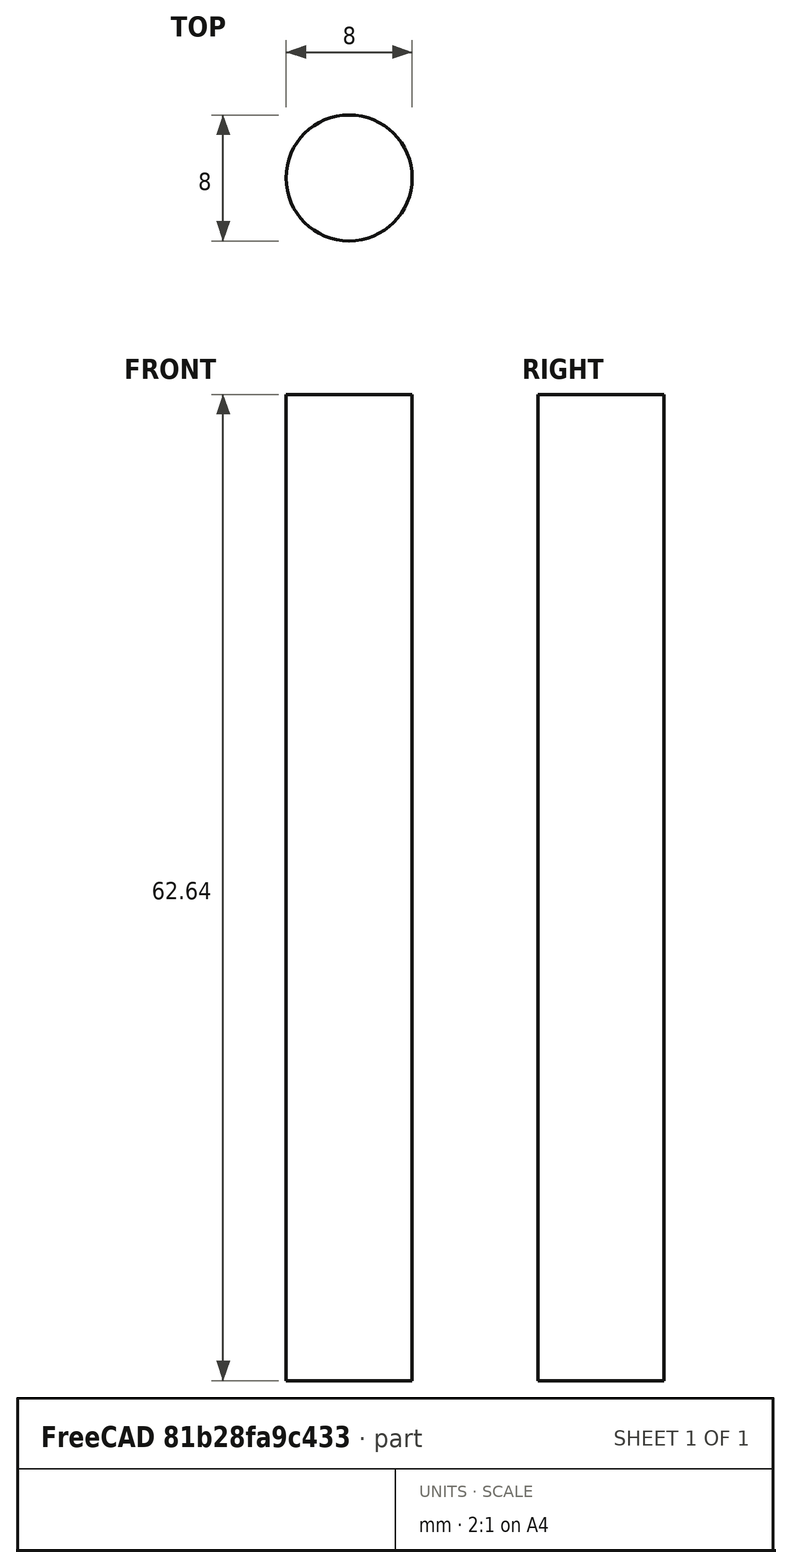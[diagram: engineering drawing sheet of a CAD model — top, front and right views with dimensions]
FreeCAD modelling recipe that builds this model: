
FCSTD DOCUMENT  (FreeCAD 1.0R39109 (Git))
Label: Studs_Frame_Base
License: All rights reserved
LicenseURL: http://en.wikipedia.org/wiki/All_rights_reserved
objects: App::Link×6, Spreadsheet::Sheet×1, Part::Cylinder×1, App::Part×1
note: 1 computed .brp shape members not serialized (recipe doc carries the construction recipe); baked Part::Feature solids carry a one-line shape summary decoded from their .brp
EXTERNAL_REF file=../../Master_of_Puppets.FCStd obj=Alternator
EXTERNAL_REF file=../../Master_of_Puppets.FCStd obj=Fastener
EXTERNAL_REF file=../../Master_of_Puppets.FCStd obj=Hub
EXTERNAL_REF file=../../Master_of_Puppets.FCStd obj=Spreadsheet
EXTERNAL_REF file=../../Fasteners/Fastener_HexNut.FCStd obj=Body
EXTERNAL_REF file=../../Fasteners/Fastener_Washer.FCStd obj=Tube

FEATURE [Spreadsheet::Sheet] Spreadsheet
  cells = A1='Inputs; A2='HolesRadius; B2(HolesRadius)==Master_of_Puppets#Alternator.HolesRadius; A3='MetalThicknessL; B3(MetalThicknessL)==Master_of_Puppets#Spreadsheet.MetalThicknessL; A4='MetalLengthL; B4(MetalLengthL)==Master_of_Puppets#Spreadsheet.MetalLengthL; A5='StatorMountingStudsLength; B5(StatorMountingStudsLength)==Master_of_Puppets#Alternator.StatorMountingStudsLength; A6='StatorThickness; B6(StatorThickness)==Master_of_Puppets#Spreadsheet.StatorThickness; A7='MechanicalClearance; B7(MechanicalClearance)==Master_of_Puppets#Spreadsheet.MechanicalClearance; A8='MagnetThickness; B8(MagnetThickness)==Master_of_Puppets#Spreadsheet.MagnetThickness; A9='RotorDiskThickness; B9(RotorDiskThickness)==Master_of_Puppets#Spreadsheet.RotorDiskThickness; A10='MiddlePadThickness; B10(MiddlePadThickness)==Master_of_Puppets#Hub.MiddlePadThickness; A11='HexNutThickness; B11(HexNutThickness)==Master_of_Puppets#Fastener.HexNutThickness; A12='WasherThickness; B12(WasherThickness)==Master_of_Puppets#Fastener.WasherThickness; A13='DistanceThreadsExtendFromNuts; B13(DistanceThreadsExtendFromNuts)==Master_of_Puppets#Fastener.DistanceThreadsExtendFromNuts; A14='RotorThickness; B14(RotorThickness)==Master_of_Puppets#Alternator.RotorThickness; A15='DistanceBetweenStatorAndFrame; B15(DistanceBetweenStatorAndFrame)==Master_of_Puppets#Alternator.DistanceBetweenStatorAndFrame; A16='Calculated; A17='DistanceBehindFrameBrackets; B17(DistanceBehindFrameBrackets)==MetalLengthL - MetalThicknessL; A18='BackFrameZ; B18(BackFrameZ)==StatorMountingStudsLength - DistanceBehindFrameBrackets; A19='FrontFrameZ; B19(FrontFrameZ)==BackFrameZ - HexNutThickness - MetalThicknessL; A20='BackStatorWasherZ; B20(BackStatorWasherZ)==BackFrameZ - MetalThicknessL - DistanceBetweenStatorAndFrame; A21='FrontStatorWasherZ; B21(FrontStatorWasherZ)==BackStatorWasherZ - StatorThickness - WasherThickness; A22='BackStatorHexNutZ; B22(BackStatorHexNutZ)==BackFrameZ - MetalThicknessL - DistanceBetweenStatorAndFrame + WasherThickness; A23='FrontStatorHexNutZ; B23(FrontStatorHexNutZ)==BackStatorWasherZ - StatorThickness - HexNutThickness - WasherThickness; A24='StudZ; B24(StudZ)==-DistanceBehindFrameBrackets + HexNutThickness + DistanceThreadsExtendFromNuts
FEATURE [Part::Cylinder] Cylinder  label="Stud"
  Angle = 360
  AttacherType = Attacher::AttachEngine3D
  FirstAngle = 0
  Height = 62.64
  Placement = pos=(0,0,-23.09) rot=(0,0,1;0rad)
  Radius = 4
  SecondAngle = 0
  expr: .Placement.Base.z = Spreadsheet.StudZ
  expr: Height = Spreadsheet.StatorMountingStudsLength
  expr: Radius = Spreadsheet.HolesRadius
FEATURE [App::Link] Link  label="HexNut_Frame_Back"
  LinkPlacement = pos=(0,0,27.64) rot=(0,0,1;0rad)
  LinkedObject = -> <external ../../Fasteners/Fastener_HexNut.FCStd>#Body
  Placement = pos=(0,0,27.64) rot=(0,0,1;0rad)
  expr: .Placement.Base.z = Spreadsheet.BackFrameZ
FEATURE [App::Link] Link001  label="HexNut_Frame_Front"
  LinkPlacement = pos=(0,0,15.73) rot=(0,0,1;0rad)
  LinkedObject = -> <external ../../Fasteners/Fastener_HexNut.FCStd>#Body
  Placement = pos=(0,0,15.73) rot=(0,0,1;0rad)
  expr: .Placement.Base.z = Spreadsheet.FrontFrameZ
FEATURE [App::Link] Link002  label="HexNut_Stator_Back"
  LinkPlacement = pos=(0,0,3.82) rot=(0,0,1;0rad)
  LinkedObject = -> <external ../../Fasteners/Fastener_HexNut.FCStd>#Body
  Placement = pos=(0,0,3.82) rot=(0,0,1;0rad)
  expr: .Placement.Base.z = Spreadsheet.BackStatorHexNutZ
FEATURE [App::Link] Link003  label="HexNut_Stator_Front"
  LinkPlacement = pos=(0,0,-18.09) rot=(0,0,1;0rad)
  LinkedObject = -> <external ../../Fasteners/Fastener_HexNut.FCStd>#Body
  Placement = pos=(0,0,-18.09) rot=(0,0,1;0rad)
  expr: .Placement.Base.z = Spreadsheet.FrontStatorHexNutZ
FEATURE [App::Link] Link004  label="Washer_Stator_Back"
  LinkPlacement = pos=(0,0,1.32) rot=(0,0,1;0rad)
  LinkedObject = -> <external ../../Fasteners/Fastener_Washer.FCStd>#Tube
  Placement = pos=(0,0,1.32) rot=(0,0,1;0rad)
  expr: .Placement.Base.z = Spreadsheet.BackStatorWasherZ
FEATURE [App::Link] Link005  label="Washer_Stator_Front"
  LinkPlacement = pos=(0,0,-11.18) rot=(0,0,1;0rad)
  LinkedObject = -> <external ../../Fasteners/Fastener_Washer.FCStd>#Tube
  Placement = pos=(0,0,-11.18) rot=(0,0,1;0rad)
  expr: .Placement.Base.z = Spreadsheet.FrontStatorWasherZ
FEATURE [App::Part] Part  label="Studs_Frame_Base"
  Group = -> [Cylinder,Link,Link001,Link002,Link003,Link004,Link005]
  Origin = -> Origin

RESOLVED EXTERNAL PARTS (link-assembly join: the EXTERNAL_REF files above that resolve inside this repo's crawl, each included once):
---- part ../../Fasteners/Fastener_HexNut.FCStd = doc fcstd_2be729c7bb98 ----
FCSTD DOCUMENT  (FreeCAD 0.21R33771 (Git))
Label: Fastener_HexNut
License: All rights reserved
LicenseURL: http://en.wikipedia.org/wiki/All_rights_reserved
objects: Sketcher::SketchObject×2, PartDesign::Chamfer×2, PartDesign::Pad×1, Spreadsheet::Sheet×1, PartDesign::Groove×1, PartDesign::Body×1
note: 11 computed .brp shape members not serialized (recipe doc carries the construction recipe); baked Part::Feature solids carry a one-line shape summary decoded from their .brp
EXTERNAL_REF file=../Master_of_Puppets.FCStd obj=Alternator
EXTERNAL_REF file=../Master_of_Puppets.FCStd obj=Hub

FEATURE [Sketcher::SketchObject] Sketch
  FullyConstrained = true
  MapMode = 5
  Support = -> [XY_Plane]
  expr: Constraints[19] = Spreadsheet.ExternalRadius
  expr: Constraints[21] = Spreadsheet.MajorRadius
  sketch-geometry (8):
    g0: LineSegment StartX=2e-16 StartY=7 StartZ=0 EndX=-6.06218 EndY=3.5 EndZ=0
    g1: LineSegment StartX=-6.06218 StartY=3.5 StartZ=0 EndX=-6.06218 EndY=-3.5 EndZ=0
    g2: LineSegment StartX=-6.06218 StartY=-3.5 StartZ=0 EndX=0 EndY=-7 EndZ=0
    g3: LineSegment StartX=2e-16 StartY=-7 StartZ=0 EndX=6.06218 EndY=-3.5 EndZ=0
    g4: LineSegment StartX=6.06218 StartY=-3.5 StartZ=0 EndX=6.06218 EndY=3.5 EndZ=0
    g5: LineSegment StartX=6.06218 StartY=3.5 StartZ=0 EndX=0 EndY=7 EndZ=0
    g6: Circle CenterX=0 CenterY=0 CenterZ=0 NormalX=0 NormalY=0 NormalZ=1 AngleXU=0 Radius=7
    g7: Circle CenterX=0 CenterY=0 CenterZ=0 NormalX=0 NormalY=0 NormalZ=1 AngleXU=0 Radius=4
  constraints (18):
    c: Coincident(g0,g1)
    c: Coincident(g1,g2)
    c: Coincident(g2,g3)
    c: Coincident(g3,g4)
    c: Coincident(g4,g5)
    c: Equal(g0, g1-g5) x5
    c: PointOnObject(g0,g6)
    c: PointOnObject(g1,g6)
    c: PointOnObject(g2,g6)
    c: PointOnObject(g3,g6)
    c: PointOnObject(g4,g6)
    c: PointOnObject(g5,g6)
    c: Coincident(g6,g-1)
    c: PointOnObject(g5,g-2)
    c: Symmetric(g0,g2,g-1)
    c: DistanceY(g-1,g0) = 7
    c: Coincident(g7,g-1)
    c: Radius(g7) = 4
FEATURE [PartDesign::Pad] Pad
  Direction = (0,0,1)
  Length = 6.91
  Length2 = 100
  Profile = -> Sketch
  Type = 0
  expr: Length = Spreadsheet.Height
FEATURE [Sketcher::SketchObject] Sketch001
  FullyConstrained = true
  MapMode = 5
  Placement = pos=(0,0,0) rot=(0.57735,0.57735,0.57735;2.0944rad)
  Support = -> [YZ_Plane]
  expr: Constraints[0] = Spreadsheet.TriangleWidth
  expr: Constraints[14] = Spreadsheet.B15
  expr: Constraints[15] = Spreadsheet.TriangleDistance
  expr: Constraints[16] = Spreadsheet.TriangleWidth
  expr: Constraints[17] = Spreadsheet.TriangleDistance
  expr: Constraints[6] = Spreadsheet.B15
  expr: Constraints[7] = Spreadsheet.Height
  sketch-geometry (6):
    g0: LineSegment StartX=-6.06218 StartY=6.91 StartZ=0 EndX=-7 EndY=6.91 EndZ=0
    g1: LineSegment StartX=-7 StartY=5.28564 StartZ=0 EndX=-7 EndY=6.91 EndZ=0
    g2: LineSegment StartX=-6.06218 StartY=6.91 StartZ=0 EndX=-7 EndY=5.28564 EndZ=0
    g3: LineSegment StartX=-7 StartY=1.62436 StartZ=0 EndX=-7 EndY=0 EndZ=0
    g4: LineSegment StartX=-7 StartY=0 StartZ=0 EndX=-6.06218 EndY=0 EndZ=0
    g5: LineSegment StartX=-7 StartY=1.62436 StartZ=0 EndX=-6.06218 EndY=0 EndZ=0
  constraints (18):
    c: DistanceX(g0,g0) = 0.937822
    c: Coincident(g0,g1)
    c: Horizontal(g0)
    c: Vertical(g1)
    c: Coincident(g2,g0)
    c: Coincident(g2,g1)
    c: Angle(g0,g2) = 1.0472
    c: DistanceY(g-1,g0) = 6.91
    c: PointOnObject(g3,g-1)
    c: Vertical(g3)
    c: Coincident(g4,g3)
    c: PointOnObject(g4,g-1)
    c: Coincident(g5,g3)
    c: Coincident(g5,g4)
    c: Angle(g5,g4) = 1.0472
    c: DistanceX(g4,g-1) = 6.06218
    c: DistanceX(g4,g4) = 0.937822
    c: DistanceX(g0,g-1) = 6.06218
FEATURE [Spreadsheet::Sheet] Spreadsheet
  cells = A1='Variant; B1='Radius; A2='HolesRadius; B2(Radius)==.B3; A3='HolesRadius; B3==Master_of_Puppets#Alternator.HolesRadius; A4='HubHolesRadius; B4==Master_of_Puppets#Hub.HubHolesRadius; A5='StatorMold; B5==Master_of_Puppets#Alternator.StatorMoldBoltDiameter / 2; A6='CoilWinder; B6==Master_of_Puppets#Alternator.CoilWinderCenterRodRadius; A8='Inputs; A9='HexNutThickness; B9(HexNutThickness)==1.64 * Radius + 0.35; A10='Parameters; A11='MajorDiameter; B11(MajorDiameter)==Radius * 2; A12='ExternalDiameter; B12(ExternalDiameter)==Radius * 3.5; A13='Height; B13(Height)==HexNutThickness; A14='Calculations; B14='See Also; C14='https://calcresource.com/geom-hexagon.html; A15='CentralAngle; B15(CentralAngle)==360 / 6; A16='Theta; B16(Theta)==CentralAngle / 2; A17='ExternalRadius; B17(ExternalRadius)==ExternalDiameter / 2; A18='Inradius; B18(Inradius)==cos(Theta) * ExternalRadius; A19='TriangleWidth; B19(TriangleWidth)==ExternalRadius - Inradius; A20='TriangleDistance; B20(TriangleDistance)==ExternalRadius - TriangleWidth; A21='MajorRadius; B21(MajorRadius)==MajorDiameter / 2; A22='Chamfer; B22(Chamfer)==HexNutThickness * 0.14
  expr: .cells.Bind.B2.B2 = tuple(.cells; <<B>> + str(hiddenref(Body.Variant) + 3); <<B>> + str(hiddenref(Body.Variant) + 3))
FEATURE [PartDesign::Chamfer] Chamfer  label="TopChamfer"
  Angle = 45
  Base = -> Pad [Edge21]
  BaseFeature = -> Pad
  ChamferType = 0
  FlipDirection = false
  Size = 0.9674
  Size2 = 1
  SupportTransform = false
  UseAllEdges = false
  expr: Size = Spreadsheet.Chamfer
FEATURE [PartDesign::Chamfer] Chamfer001  label="BottomChamfer"
  Angle = 45
  Base = -> Chamfer [Edge3]
  BaseFeature = -> Chamfer
  ChamferType = 0
  FlipDirection = false
  Size = 0.9674
  Size2 = 1
  SupportTransform = false
  UseAllEdges = false
  expr: Size = Spreadsheet.Chamfer
FEATURE [PartDesign::Groove] Groove
  Angle = 360
  Axis = (-3e-16,3e-16,1)
  Base = (0,0,0)
  BaseFeature = -> Chamfer001
  Midplane = true
  Profile = -> Sketch001
  ReferenceAxis = -> Z_Axis
  Reversed = true
FEATURE [PartDesign::Body] Body  label="Fastener_HexNut"
  Group = -> [Sketch,Pad,Chamfer,Chamfer001,Sketch001,Groove]
  Origin = -> Origin
  Tip = -> Groove
  Variant = 0
  expr: .Variant.Enum = Spreadsheet.cells[<<A3:|>>]
---- part ../../Master_of_Puppets.FCStd = doc fcstd_6404554055c4 (61625 chars; too large to inline — full recipe in that document) ----
